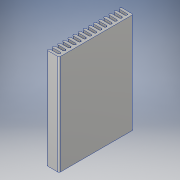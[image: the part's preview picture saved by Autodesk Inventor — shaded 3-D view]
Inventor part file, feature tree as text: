
AUTODESK INVENTOR PART (.ipt)
format: ipt  version: 2019 (Build 230136000, 136)  size: 278,528 bytes
history: native  units: mm
features: fillet x7, other x2, extrude x2, sketch x2, pattern_linear x1
ambient origin geometry x8: Origin, YZ Plane, XZ Plane, XY Plane, X Axis, Y Axis, Z Axis, Center Point
bodies: Body1 (feature_tree)
feature tree (14):
  other  "Bryła1"
  extrude  "Wyciągnięcie proste1"  Depth=10.0mm
  extrude  "Wyciągnięcie proste2"  Depth=5.0mm
  pattern_linear  "Szyk prostokątny1"  Count1=6  [1 undecoded]
  fillet  "Zaokrąglenie1"  Radius=30.0mm
  fillet  "Zaokrąglenie2"  Radius=100.0mm
  fillet  "Zaokrąglenie3"  Radius=2.0mm
  fillet  "Zaokrąglenie4"  Radius=2.0mm
  fillet  "Zaokrąglenie5"  Radius=2.0mm
  fillet  "Zaokrąglenie6"  Radius=100.0mm
  fillet  "Zaokrąglenie7"  Radius=4.15mm
  other  "Pogrubienie1"
  sketch  "Szkic1"
  sketch  "Szkic2"
note: 1 required parameter value undecoded (feature->parameter linkage not recoverable at this tier; creation-order binding heuristic only, values carry confidence <= 0.55)
